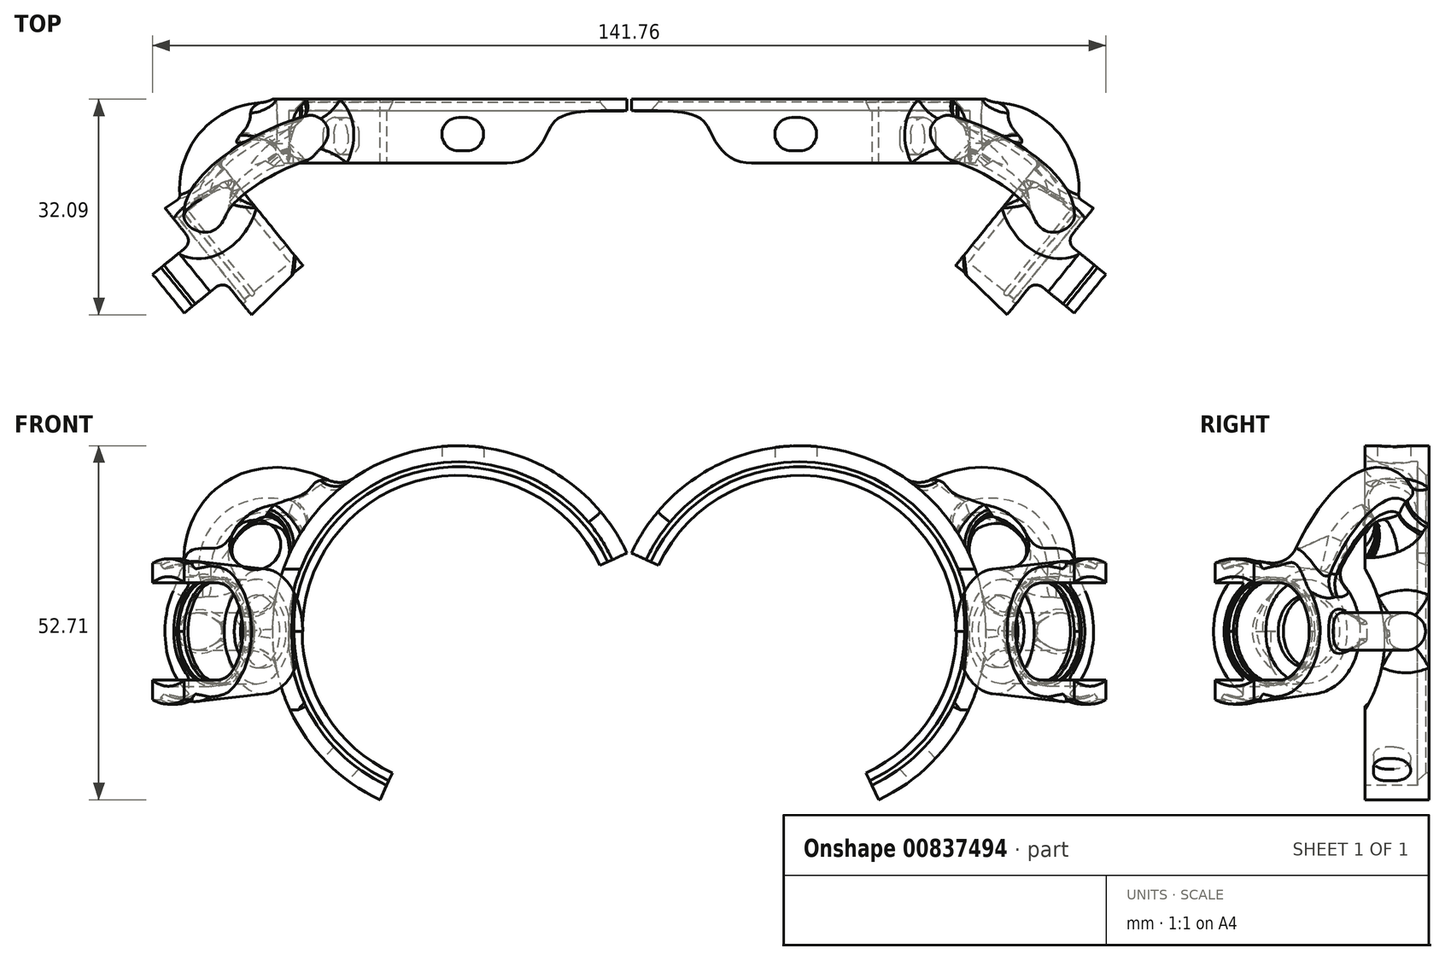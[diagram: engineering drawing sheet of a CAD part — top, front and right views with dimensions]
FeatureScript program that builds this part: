
annotation { "Feature Type Name" : "Feature", "Feature Type Description" : "" }
export const myFeature = defineFeature(function(context is Context, id is Id, definition is map)
    precondition{}
    {
        {
            var Q0;
            Q0=qCreatedBy(makeId("Front.planeOp"),FACE);
            var sketch = newSketch(context, id + "F0", { "sketchPlane" : qUnion([Q0])});
            skCircle(sketch, "E0", {"center": v(0, 0) * mm, "radius": 25.27 * mm, "construction": true});
            skCircle(sketch, "E1", {"center": v(0, 0) * mm, "radius": 23.24 * mm, "construction": true});
            skLineSegment(sketch, "E2", {"start": v(0, 0) * mm, "end": v(0, 25.27) * mm, "construction": true});
            skLineSegment(sketch, "E3", {"start": v(0, 0) * mm, "end": v(25.27, 0) * mm, "construction": true});
            skLineSegment(sketch, "E4", {"start": v(0, 0) * mm, "end": v(17.87, 17.87) * mm, "construction": true});
            skCircle(sketch, "E5", {"center": v(0, 0) * mm, "radius": 15.88 * mm, "construction": true});
            skPoint(sketch, "E6", {"position": v(17.87, 17.86) * mm});
            skLineSegment(sketch, "E7", {"start": v(0, 0) * mm, "end": v(16.74, -18.92) * mm, "construction": true});
            skPoint(sketch, "E8", {"position": v(17.88, -17.85) * mm});
            skSolve(sketch);
        }
        {
            var Q0;
            Q0=qCreatedBy(makeId("Right.planeOp"),FACE);
            var sketch = newSketch(context, id + "F1", { "sketchPlane" : qUnion([Q0])});
            skLineSegment(sketch, "E9.0", {"start": v(0, -25.27) * mm, "end": v(0, 25.27) * mm, "construction": true});
            skLineSegment(sketch, "E9.1", {"start": v(0, -23.24) * mm, "end": v(0, 23.24) * mm, "construction": true});
            skLineSegment(sketch, "E10", {"start": v(0, 23.24) * mm, "end": v(-1.73, 23.24) * mm});
            skLineSegment(sketch, "E11", {"start": v(-1.73, 23.24) * mm, "end": v(-1.73, 25.27) * mm});
            skLineSegment(sketch, "E12", {"start": v(-1.73, 25.27) * mm, "end": v(-9.53, 25.27) * mm});
            skLineSegment(sketch, "E13", {"start": v(0, 23.24) * mm, "end": v(0, 25.27) * mm});
            skLineSegment(sketch, "E14", {"start": v(-9.53, 25.27) * mm, "end": v(-9.53, 27.65) * mm});
            skLineSegment(sketch, "E15", {"start": v(-9.53, 27.65) * mm, "end": v(0, 27.65) * mm});
            skLineSegment(sketch, "E16", {"start": v(0, 27.65) * mm, "end": v(0, 25.27) * mm});
            skLineSegment(sketch, "E17", {"start": v(0, 0) * mm, "end": v(1.7, 0) * mm, "construction": true});
            skLineSegment(sketch, "E18.0", {"start": v(0, -15.88) * mm, "end": v(0, 15.88) * mm, "construction": true});
            skLineSegment(sketch, "E19", {"start": v(0, 15.88) * mm, "end": v(5.77, 15.88) * mm, "construction": true});
            skLineSegment(sketch, "E20", {"start": v(0, -15.88) * mm, "end": v(5.77, -15.88) * mm, "construction": true});
            skLineSegment(sketch, "E21", {"start": v(0, 27.65) * mm, "end": v(-14.29, 27.65) * mm, "construction": true});
            skLineSegment(sketch, "E22", {"start": v(0, -25.27) * mm, "end": v(-14.29, -25.27) * mm, "construction": true});
            skLineSegment(sketch, "E23", {"start": v(5.77, 15.88) * mm, "end": v(5.77, -15.88) * mm, "construction": true});
            skLineSegment(sketch, "E24", {"start": v(6.02, 0) * mm, "end": v(18.72, 0) * mm});
            skPoint(sketch, "E25", {"position": v(-5.16, 27.65) * mm});
            skSolve(sketch);
        }
        {
            var Q0;
            Q0=makeQuery(id+"F1.imprint","IMPRINT",FACE,{"disambiguationData":[TD([[makeQuery(id+"F1.imprint","IMPRINT",EDGE,{"derivedFrom":sQuery(id+"F1.wireOp",EDGE,"E10")}),-1.0]])]});
            var Q1;
            Q1=sQuery(id+"F1.wireOp",EDGE,"E17");
            revolve(context, id + "F2", {"surfaceOperationType" : NewSurfaceOperationType.NEW, "entities" : qUnion([Q0]), "axis" : qUnion([Q1]), "revolveType" : RevolveType.TWO_DIRECTIONS, "angle" : 115 * degree, "angleBack" : 310 * degree});
        }
        {
            var Q0;
            Q0=qCreatedBy(makeId("Top.planeOp"),FACE);
            var sketch = newSketch(context, id + "F3", { "sketchPlane" : qUnion([Q0])});
            skLineSegment(sketch, "E26.0", {"start": v(0, 6.02) * mm, "end": v(0, 18.72) * mm});
            skLineSegment(sketch, "E26.1.0", {"start": v(-21.18, -9.53) * mm, "end": v(27.65, -9.53) * mm});
            skLineSegment(sketch, "E26.1.1", {"start": v(25.06, -9.53) * mm, "end": v(25.06, 0) * mm});
            skLineSegment(sketch, "E26.1.2", {"start": v(27.65, 0) * mm, "end": v(-21.18, 0) * mm});
            skLineSegment(sketch, "E26.1.3", {"start": v(-21.18, 0) * mm, "end": v(-21.18, -9.53) * mm});
            skLineSegment(sketch, "E27", {"start": v(0, 6.02) * mm, "end": v(4.9, 12.06) * mm, "construction": true});
            skLineSegment(sketch, "E28", {"start": v(0, 6.02) * mm, "end": v(25.06, -14.29) * mm, "construction": true});
            skLineSegment(sketch, "E29", {"start": v(4.9, 12.06) * mm, "end": v(34.84, -12.22) * mm, "construction": true});
            skLineSegment(sketch, "E30", {"start": v(25.06, -9.53) * mm, "end": v(25.06, -19.05) * mm, "construction": true});
            skLineSegment(sketch, "E31.MirrorCS", {"start": v(-4.9, -0.02) * mm, "end": v(25.06, -24.3) * mm, "construction": true});
            skLineSegment(sketch, "E32.MirrorCS", {"start": v(0, 6.02) * mm, "end": v(-4.9, -0.02) * mm, "construction": true});
            skLineSegment(sketch, "E33", {"start": v(25.06, -19.05) * mm, "end": v(25.06, -24.3) * mm});
            skLineSegment(sketch, "E34", {"start": v(25.06, -24.3) * mm, "end": v(34.84, -12.22) * mm, "construction": true});
            skLineSegment(sketch, "E35", {"start": v(34.84, -12.22) * mm, "end": v(33.35, -14.07) * mm});
            skLineSegment(sketch, "E36", {"start": v(33.35, -14.07) * mm, "end": v(32.42, -13.32) * mm});
            skLineSegment(sketch, "E37", {"start": v(34.84, -12.22) * mm, "end": v(41.63, -17.71) * mm});
            skLineSegment(sketch, "E38", {"start": v(41.63, -17.71) * mm, "end": v(42.59, -16.53) * mm});
            skLineSegment(sketch, "E39", {"start": v(42.59, -16.53) * mm, "end": v(34.88, -10.28) * mm});
            skLineSegment(sketch, "E40", {"start": v(32.42, -13.32) * mm, "end": v(34.88, -10.28) * mm});
            skLineSegment(sketch, "E41", {"start": v(41.87, -17.42) * mm, "end": v(48.28, -22.61) * mm});
            skLineSegment(sketch, "E42", {"start": v(42.59, -16.53) * mm, "end": v(49, -21.73) * mm});
            skLineSegment(sketch, "E43", {"start": v(48.28, -22.61) * mm, "end": v(49, -21.73) * mm});
            skLineSegment(sketch, "E44", {"start": v(29.95, -18.25) * mm, "end": v(32.08, -19.98) * mm, "construction": true});
            skLineSegment(sketch, "E45", {"start": v(49, -21.73) * mm, "end": v(49.96, -20.54) * mm});
            skLineSegment(sketch, "E46", {"start": v(49.96, -20.54) * mm, "end": v(48.73, -19.54) * mm});
            skLineSegment(sketch, "E47", {"start": v(48.73, -19.54) * mm, "end": v(47.77, -20.73) * mm});
            skLineSegment(sketch, "E48", {"start": v(34.76, -12.31) * mm, "end": v(41.63, -17.71) * mm});
            skLineSegment(sketch, "E49", {"start": v(45.1, -18.57) * mm, "end": v(45.82, -17.68) * mm});
            skLineSegment(sketch, "E50", {"start": v(45.82, -17.68) * mm, "end": v(34.88, -10.28) * mm});
            skCircle(sketch, "E51", {"center": v(40.5, -16.8) * mm, "radius": 0.37 * mm});
            skLineSegment(sketch, "E52", {"start": v(45.82, -17.68) * mm, "end": v(48.17, -20.23) * mm});
            skSolve(sketch);
        }
        {
            var Q0;
            Q0=makeQuery(id+"F3.imprint","IMPRINT",FACE,{"disambiguationData":[TD([[makeQuery(id+"F3.imprint","IMPRINT",EDGE,{"derivedFrom":sQuery(id+"F3.wireOp",EDGE,"E35")}),-1.0]])]});
            var Q1;
            {var subQ2=sQuery(id+"F3.wireOp",EDGE,"E41");Q1=makeQuery(id+"F3.imprint","IMPRINT",FACE,{"disambiguationData":[TD([[makeQuery(id+"F3.imprint","IMPRINT",EDGE,{"derivedFrom":subQ2}),1.0]])]});}
            var Q2;
            {var subQ0=sQuery(id+"F3.wireOp",EDGE,"E45");Q2=makeQuery(id+"F3.imprint","IMPRINT",FACE,{"disambiguationData":[TD([[makeQuery(id+"F3.imprint","IMPRINT",EDGE,{"derivedFrom":subQ0}),1.0]])]});}
            var Q3;
            {var subQ0=sQuery(id+"F3.wireOp",EDGE,"ZS8Crhrf-CrOi-06I2-Trp5-8wOd5zCYoBhE");Q3=makeQuery(id+"F3.imprint","IMPRINT",FACE,{"disambiguationData":[TD([[makeQuery(id+"F3.imprint","IMPRINT",EDGE,{"derivedFrom":subQ0}),-1.0]])]});}
            var Q4;
            {var subQ0=sQuery(id+"F3.wireOp",EDGE,"E39");Q4=makeQuery(id+"F3.imprint","IMPRINT",FACE,{"disambiguationData":[TD([[makeQuery(id+"F3.imprint","IMPRINT",EDGE,{"derivedFrom":subQ0}),-1.0]])]});}
            var Q5;
            {var subQ0=sQuery(id+"F3.wireOp",EDGE,"E51");var subQ1=sQuery(id+"F3.wireOp",EDGE,"E37");var subQ2=makeQuery(id+"F3.imprint","INTERSECT",VERTEX,{"disambiguationData":[OD(0.0)],"derivedFrom":[subQ1,subQ0]});Q5=makeQuery(id+"F3.imprint","IMPRINT",FACE,{"disambiguationData":[TD([[makeQuery(id+"F3.imprint","IMPRINT",EDGE,{"disambiguationData":[TD([[subQ2,-1.0]])],"derivedFrom":subQ1}),1.0]])]});}
            var Q6;
            {var subQ5=sQuery(id+"F3.wireOp",EDGE,"J8IAMYAS-e4tZ-yNnO-T2ef-1q77QjKvg4NF");Q6=makeQuery(id+"F3.imprint","IMPRINT",FACE,{"disambiguationData":[TD([[makeQuery(id+"F3.imprint","IMPRINT",EDGE,{"derivedFrom":subQ5}),-1.0]])]});}
            var Q7;
            {var subQ3=sQuery(id+"F3.wireOp",EDGE,"E49");Q7=makeQuery(id+"F3.imprint","IMPRINT",FACE,{"disambiguationData":[TD([[makeQuery(id+"F3.imprint","IMPRINT",EDGE,{"derivedFrom":subQ3}),-1.0]])]});}
            var Q8;
            Q8=sQuery(id+"F3.wireOp",EDGE,"E44");
            var Q9;
            Q9=sQuery(id+"F3.wireOp",EDGE,"E44");
            revolve(context, id + "F4", {"operationType" : NewBodyOperationType.ADD, "surfaceOperationType" : NewSurfaceOperationType.NEW, "entities" : qUnion([Q0, Q1, Q2, Q3, Q4, Q5, Q6, Q7]), "surfaceEntities" : qUnion([Q8]), "axis" : qUnion([Q9]), "revolveType" : RevolveType.FULL});
        }
        {
            var Q0;
            Q0=makeQuery(id+"F4.opRevolve","SWEPT_FACE",FACE,{"disambiguationData":[OSD([sQuery(id+"F3.wireOp",EDGE,"E35")])]});
            var sketch = newSketch(context, id + "F5", { "sketchPlane" : qUnion([Q0])});
            skCircle(sketch, "E53.0", {"center": v(4.68, 0) * mm, "radius": 5.4 * mm, "construction": true});
            skLineSegment(sketch, "E54", {"start": v(4.68, 0) * mm, "end": v(4.68, 5.4) * mm, "construction": true});
            skLineSegment(sketch, "E55", {"start": v(4.68, 0) * mm, "end": v(6.74, 4.98) * mm, "construction": true});
            skSolve(sketch);
        }
        {
            var Q0;
            Q0=qCreatedBy(makeId("Right.planeOp"),FACE);
            var sketch = newSketch(context, id + "F6", { "sketchPlane" : qUnion([Q0])});
            skEllipse(sketch, "E56.0", {"center": v(-17.5, 0) * mm, "majorRadius": 8.76 * mm, "minorRadius": 5.18 * mm, "majorAxis": v(0, -1), "construction": true});
            skLineSegment(sketch, "E56.1.0", {"start": v(-9.53, 27.65) * mm, "end": v(-9.53, -11.68) * mm, "construction": true});
            skLineSegment(sketch, "E56.1.1", {"start": v(-9.53, -11.68) * mm, "end": v(0, -11.68) * mm});
            skLineSegment(sketch, "E56.1.2", {"start": v(0, -11.68) * mm, "end": v(0, 27.65) * mm});
            skLineSegment(sketch, "E56.1.3", {"start": v(0, 17.77) * mm, "end": v(-9.53, 17.77) * mm, "construction": true});
            skLineSegment(sketch, "E57", {"start": v(-17.5, 0) * mm, "end": v(-9.53, 0) * mm, "construction": true});
            skLineSegment(sketch, "E58", {"start": v(-17.5, 9.3) * mm, "end": v(-9.53, 9.3) * mm, "construction": true});
            skLineSegment(sketch, "E59", {"start": v(-17.5, -9.3) * mm, "end": v(-9.53, -9.3) * mm, "construction": true});
            skLineSegment(sketch, "E60", {"start": v(-9.53, 9.3) * mm, "end": v(-9.53, -9.3) * mm});
            skArc(sketch, "E61", {"start": v(-9.52, -11.68) * mm, "mid": v(-6.6, -1.2) * mm, "end": v(-9.52, 9.3) * mm});
            skLineSegment(sketch, "E62", {"start": v(-9.53, -9.3) * mm, "end": v(-9.53, -11.68) * mm});
            skSolve(sketch);
        }
        {
            var Q0;
            Q0=makeQuery(id+"F6.imprint","IMPRINT",FACE,{"disambiguationData":[TD([[makeQuery(id+"F6.imprint","IMPRINT",EDGE,{"derivedFrom":sQuery(id+"F6.wireOp",EDGE,"GxEW9ax0-zjAY-ybk5-duMN-0JDvZg63hfbD")}),1.0]])]});
            var Q1;
            Q1=makeQuery(id+"F6.imprint","IMPRINT",FACE,{"disambiguationData":[TD([[makeQuery(id+"F6.imprint","IMPRINT",EDGE,{"derivedFrom":sQuery(id+"F6.wireOp",EDGE,"E60")}),1.0]])]});
            extrude(context, id + "F7", {"entities" : qUnion([Q0, Q1]), "operationType" : NewBodyOperationType.REMOVE, "depth" : 50.57 * mm, "offsetDistance" : 25.4 * mm});
        }
        {
            var Q0;
            Q0=qCreatedBy(makeId("Top.planeOp"),FACE);
            var sketch = newSketch(context, id + "F8", { "sketchPlane" : qUnion([Q0])});
            skLineSegment(sketch, "E63.1.0", {"start": v(-21.18, -9.53) * mm, "end": v(26.26, -9.53) * mm, "construction": true});
            skLineSegment(sketch, "E63.1.2", {"start": v(25.06, -11.07) * mm, "end": v(25.06, 0) * mm, "construction": true});
            skLineSegment(sketch, "E63.1.3", {"start": v(27.65, 0) * mm, "end": v(-21.18, 0) * mm, "construction": true});
            skLineSegment(sketch, "E63.1.4", {"start": v(-21.18, 0) * mm, "end": v(-21.18, -9.53) * mm});
            skLineSegment(sketch, "E64.0", {"start": v(25.63, -21.7) * mm, "end": v(32.42, -13.32) * mm, "construction": true});
            skLineSegment(sketch, "E64.1", {"start": v(23.17, -24.73) * mm, "end": v(34.88, -10.28) * mm, "construction": true});
            skLineSegment(sketch, "E64.3", {"start": v(31.84, -29.79) * mm, "end": v(41.63, -17.71) * mm, "construction": true});
            skLineSegment(sketch, "E64.4", {"start": v(25.06, -24.3) * mm, "end": v(34.84, -12.22) * mm, "construction": true});
            skLineSegment(sketch, "E65", {"start": v(34.84, -12.22) * mm, "end": v(41.63, -17.71) * mm, "construction": true});
            skPoint(sketch, "E66", {"position": v(25.06, -3.81) * mm});
            skPoint(sketch, "E66.positionSnap0", {"position": v(27.71, -3.81) * mm});
            skArc(sketch, "E67", {"start": v(38.8, -14.27) * mm, "mid": v(34.84, -5.22) * mm, "end": v(25.06, -3.81) * mm});
            skLineSegment(sketch, "E68", {"start": v(34.84, -12.22) * mm, "end": v(35.4, -11.52) * mm});
            skLineSegment(sketch, "E69", {"start": v(35.4, -11.52) * mm, "end": v(42.19, -17.02) * mm});
            skLineSegment(sketch, "E70", {"start": v(42.19, -17.02) * mm, "end": v(41.63, -17.71) * mm});
            skSolve(sketch);
        }
        {
            var Q0;
            Q0=sQuery(id+"F8.wireOp",EDGE,"E63.1.2");
            cPlane(context, id + "F9", {"entities" : qUnion([Q0]), "cplaneType" : CPlaneType.LINE_ANGLE, "offset" : 25.4 * mm, "angle" : 90 * degree, "width" : 152.4 * mm, "height" : 152.4 * mm});
        }
        {
            var Q0;
            Q0=qCreatedBy(id+"F9.planeOp",FACE);
            var sketch = newSketch(context, id + "F10", { "sketchPlane" : qUnion([Q0])});
            skPoint(sketch, "E71.0", {"position": v(-3.81, 0) * mm});
            skCircle(sketch, "E72", {"center": v(-3.81, 0) * mm, "radius": 2.8 * mm});
            skSolve(sketch);
        }
        {
            var Q0;
            Q0=qSketchRegion(id+"F10",true);
            var Q1;
            Q1=sQuery(id+"F8.wireOp",EDGE,"E67");
            sweep(context, id + "F11", {"operationType" : NewBodyOperationType.ADD, "profiles" : qUnion([Q0]), "path" : qUnion([Q1])});
        }
        {
            var Q0;
            Q0=makeQuery(id+"F2.opRevolve","SWEPT_FACE",FACE,{"disambiguationData":[OSD([sQuery(id+"F1.wireOp",EDGE,"E11")])]});
            var sketch = newSketch(context, id + "F12", { "sketchPlane" : qUnion([Q0])});
            skPoint(sketch, "E73.0", {"position": v(17.87, 17.86) * mm});
            skSolve(sketch);
        }
        {
            var Q0;
            Q0=sQuery(id+"F12.wireOp",VERTEX,"E73.0");
            var Q1;
            Q1=sQuery(id+"F0.wireOp",VERTEX,"E4.end");
            var Q2;
            Q2=sQuery(id+"F0.wireOp",VERTEX,"E6");
            cPlane(context, id + "F13", {"entities" : qUnion([Q0, Q1, Q2]), "cplaneType" : CPlaneType.THREE_POINT, "offset" : 25.4 * mm, "width" : 152.4 * mm, "height" : 152.4 * mm});
        }
        {
            var Q0;
            Q0=qCreatedBy(id+"F13.planeOp",FACE);
            var sketch = newSketch(context, id + "F14", { "sketchPlane" : qUnion([Q0])});
            skLineSegment(sketch, "E74", {"start": v(0, 0) * mm, "end": v(-9.53, 0) * mm, "construction": true});
            skLineSegment(sketch, "E75.0", {"start": v(-9.53, -5.93) * mm, "end": v(-9.53, 27.65) * mm, "construction": true});
            skCircle(sketch, "E76", {"center": v(-4.76, 0) * mm, "radius": 3.18 * mm});
            skLineSegment(sketch, "E77", {"start": v(-4.76, 0) * mm, "end": v(-4.76, 3.18) * mm, "construction": true});
            skLineSegment(sketch, "E78", {"start": v(-4.76, 3.18) * mm, "end": v(-4.76, -3.18) * mm, "construction": true});
            skCircle(sketch, "E79", {"center": v(-4.76, -3.18) * mm, "radius": 1.59 * mm});
            skSolve(sketch);
        }
        {
            var Q0;
            Q0=sQuery(id+"F14.wireOp",EDGE,"E74");
            cPoint(context, id + "F15", {"entities" : qUnion([Q0]), "parameter" : 0.5});
        }
        {
            var Q0;
            Q0=qCreatedBy(id+"F15",VERTEX);
            var Q1;
            Q1=sQuery(id+"F5.wireOp",VERTEX,"E54.start");
            var Q2;
            Q2=sQuery(id+"F5.wireOp",VERTEX,"E55.end");
            cPlane(context, id + "F16", {"entities" : qUnion([Q0, Q1, Q2]), "cplaneType" : CPlaneType.THREE_POINT, "offset" : 25.4 * mm, "width" : 152.4 * mm, "height" : 152.4 * mm});
        }
        {
            var Q0;
            Q0=qCreatedBy(id+"F16.planeOp",FACE);
            var sketch = newSketch(context, id + "F17", { "sketchPlane" : qUnion([Q0])});
            skPoint(sketch, "E80.0", {"position": v(-20.97, 14.4) * mm});
            skArc(sketch, "E81", {"start": v(-20.97, 14.4) * mm, "mid": v(-36.67, 14.03) * mm, "end": v(-42.1, -0.7) * mm});
            skEllipse(sketch, "E82.0", {"center": v(-34.09, -7.39) * mm, "majorRadius": 7.62 * mm, "minorRadius": 1.65 * mm, "majorAxis": v(0.26, -0.97), "construction": true});
            skEllipse(sketch, "E82.1", {"center": v(-45.34, -10.43) * mm, "majorRadius": 10.03 * mm, "minorRadius": 2.17 * mm, "majorAxis": v(0.26, -0.97), "construction": true});
            skLineSegment(sketch, "E83", {"start": v(-36.12, 0.12) * mm, "end": v(-48.07, -0.36) * mm, "construction": true});
            skPoint(sketch, "E84", {"position": v(-42.1, -0.12) * mm});
            skSolve(sketch);
        }
        {
            var Q0;
            Q0=qSketchRegion(id+"F14",true);
            var Q1;
            Q1=sQuery(id+"F17.wireOp",EDGE,"E81");
            sweep(context, id + "F18", {"operationType" : NewBodyOperationType.ADD, "profiles" : qUnion([Q0]), "path" : qUnion([Q1])});
        }
        {
            var Q0;
            Q0=qCreatedBy(makeId("Top.planeOp"),FACE);
            var sketch = newSketch(context, id + "F19", { "sketchPlane" : qUnion([Q0])});
            skLineSegment(sketch, "E85.0", {"start": v(31.6, -30.09) * mm, "end": v(41.87, -17.42) * mm, "construction": true});
            skLineSegment(sketch, "E86.0", {"start": v(22.9, -1.73) * mm, "end": v(22.9, -1.73) * mm});
            skLineSegment(sketch, "E87.0", {"start": v(-21.18, -9.53) * mm, "end": v(-21.18, 0) * mm, "construction": true});
            skLineSegment(sketch, "E87.1", {"start": v(-7.2, -9.53) * mm, "end": v(-21.18, -9.53) * mm, "construction": true});
            skLineSegment(sketch, "E88", {"start": v(-21.18, -1.73) * mm, "end": v(-25.57, -1.73) * mm});
            skLineSegment(sketch, "E89", {"start": v(-25.57, -1.73) * mm, "end": v(-25.57, -14.68) * mm});
            skLineSegment(sketch, "E90", {"start": v(-25.57, -14.68) * mm, "end": v(-7.2, -14.68) * mm});
            skLineSegment(sketch, "E91", {"start": v(-7.2, -14.68) * mm, "end": v(-7.2, -9.53) * mm});
            skFitSpline(sketch, "E92", {"points": [v(41.87, -17.42) * mm, v(35.6, -32.32) * mm, v(36.33, -37.36) * mm], "startDerivative": vector(-14.07, -17.37) * mm, "endDerivative": vector(-39.72, -35.09) * mm, "construction": true});
            skLineSegment(sketch, "E93", {"start": v(41.87, -17.42) * mm, "end": v(44.14, -15.47) * mm});
            skLineSegment(sketch, "E94", {"start": v(44.14, -15.47) * mm, "end": v(53.33, -26.22) * mm});
            skLineSegment(sketch, "E95", {"start": v(53.33, -26.22) * mm, "end": v(38.1, -39.23) * mm});
            skLineSegment(sketch, "E96", {"start": v(38.1, -39.23) * mm, "end": v(36.33, -37.36) * mm});
            skFitSpline(sketch, "E97", {"points": [v(-21.18, -1.73) * mm, v(-12.95, -5.57) * mm, v(-7.2, -9.53) * mm], "startDerivative": vector(39.3, 0) * mm, "endDerivative": vector(20.69, 0) * mm});
            skSolve(sketch);
        }
        {
            var Q0;
            Q0=qSketchRegion(id+"F19",true);
            extrude(context, id + "F20", {"entities" : qUnion([Q0]), "operationType" : NewBodyOperationType.REMOVE, "endBound" : BoundingType.SYMMETRIC, "oppositeDirection" : true, "depth" : 82.8 * mm, "offsetDistance" : 25.4 * mm});
        }
        {
            var Q0;
            Q0=qCreatedBy(makeId("Top.planeOp"),FACE);
            var sketch = newSketch(context, id + "F21", { "sketchPlane" : qUnion([Q0])});
            skCircle(sketch, "E98", {"center": v(0, -5.2) * mm, "radius": 2.48 * mm});
            skCircle(sketch, "E99", {"center": v(-1.27, -5.2) * mm, "radius": 2.48 * mm});
            skLineSegment(sketch, "E100", {"start": v(-1.27, -2.73) * mm, "end": v(0, -2.73) * mm});
            skLineSegment(sketch, "E101", {"start": v(-1.27, -7.68) * mm, "end": v(0, -7.68) * mm});
            skSolve(sketch);
        }
        {
            var Q0;
            Q0=makeQuery(id+"F21.imprint","IMPRINT",FACE,{"disambiguationData":[TD([[makeQuery(id+"F21.imprint","IMPRINT",EDGE,{"derivedFrom":sQuery(id+"F21.wireOp",EDGE,"E98")}),1.0]])]});
            var Q1;
            {var subQ0=sQuery(id+"F21.wireOp",EDGE,"E99");var subQ1=sQuery(id+"F21.wireOp",EDGE,"E98");var subQ2=makeQuery(id+"F21.imprint","INTERSECT",VERTEX,{"disambiguationData":[OD(0.0)],"derivedFrom":[subQ1,subQ0]});Q1=makeQuery(id+"F21.imprint","IMPRINT",FACE,{"disambiguationData":[TD([[makeQuery(id+"F21.imprint","IMPRINT",EDGE,{"disambiguationData":[TD([[subQ2,-1.0]])],"derivedFrom":subQ1}),-1.0]])]});}
            var Q2;
            {var subQ0=sQuery(id+"F21.wireOp",EDGE,"E99");var subQ1=sQuery(id+"F21.wireOp",EDGE,"E98");var subQ2=makeQuery(id+"F21.imprint","INTERSECT",VERTEX,{"disambiguationData":[OD(0.0)],"derivedFrom":[subQ1,subQ0]});Q2=makeQuery(id+"F21.imprint","IMPRINT",FACE,{"disambiguationData":[TD([[makeQuery(id+"F21.imprint","IMPRINT",EDGE,{"disambiguationData":[TD([[subQ2,-1.0]])],"derivedFrom":subQ1}),1.0]])]});}
            var Q3;
            {var subQ0=sQuery(id+"F21.wireOp",EDGE,"E100");Q3=makeQuery(id+"F21.imprint","IMPRINT",FACE,{"disambiguationData":[TD([[makeQuery(id+"F21.imprint","IMPRINT",EDGE,{"derivedFrom":subQ0}),-1.0]])]});}
            var Q4;
            {var subQ0=sQuery(id+"F21.wireOp",EDGE,"E101");Q4=makeQuery(id+"F21.imprint","IMPRINT",FACE,{"disambiguationData":[TD([[makeQuery(id+"F21.imprint","IMPRINT",EDGE,{"derivedFrom":subQ0}),1.0]])]});}
            extrude(context, id + "F22", {"entities" : qUnion([Q0, Q1, Q2, Q3, Q4]), "operationType" : NewBodyOperationType.REMOVE, "depth" : 31.5 * mm, "offsetDistance" : 25.4 * mm});
        }
        {
            var Q0;
            Q0=makeQuery(id+"F2.opRevolve","SWEPT_FACE",FACE,{"disambiguationData":[OSD([sQuery(id+"F1.wireOp",EDGE,"E11")])]});
            var sketch = newSketch(context, id + "F23", { "sketchPlane" : qUnion([Q0])});
            skArc(sketch, "E102.0", {"start": v(22.9, -10.68) * mm, "mid": v(24.44, -6.4) * mm, "end": v(25.2, -1.9) * mm});
            skCircle(sketch, "E103", {"center": v(0, 0) * mm, "radius": 24.48 * mm});
            skArc(sketch, "E104.0", {"start": v(25.2, 1.9) * mm, "mid": v(-25.27, 0) * mm, "end": v(25.2, -1.9) * mm});
            skPoint(sketch, "E105.0", {"position": v(17.87, 17.86) * mm});
            skCircle(sketch, "E106", {"center": v(0, 0) * mm, "radius": 25.27 * mm});
            skSolve(sketch);
        }
        {
            var Q0;
            {var subQ1=sQuery(id+"F1.wireOp",EDGE,"E11");var subQ6=makeQuery(id+"F2.opRevolve","SWEPT_EDGE",EDGE,{"disambiguationData":[OSD([sQuery(id+"F1.wireOp",EDGE,"E10"),subQ1])]});Q0=makeQuery(id+"F23.imprint","IMPRINT",FACE,{"disambiguationData":[TD([[makeQuery(id+"F23.imprint","IMPRINT",EDGE,{"derivedFrom":subQ6}),1.0]])]});}
            var Q1;
            {var subQ1=sQuery(id+"F1.wireOp",EDGE,"E11");var subQ6=makeQuery(id+"F2.opRevolve","SWEPT_EDGE",EDGE,{"disambiguationData":[OSD([sQuery(id+"F1.wireOp",EDGE,"E10"),subQ1])]});Q1=makeQuery(id+"F23.imprint","IMPRINT",FACE,{"disambiguationData":[TD([[makeQuery(id+"F23.imprint","IMPRINT",EDGE,{"derivedFrom":subQ6}),-1.0]])]});}
            extrude(context, id + "F24", {"entities" : qUnion([Q0, Q1]), "operationType" : NewBodyOperationType.REMOVE, "depth" : 43.43 * mm, "offsetDistance" : 25.4 * mm});
        }
        {
            var Q0;
            Q0=makeQuery(id+"F2.opRevolve","CAP_FACE",FACE,{"disambiguationData":[OSD([sQuery(id+"F1.wireOp",EDGE,"E10"),sQuery(id+"F1.wireOp",EDGE,"E11"),sQuery(id+"F1.wireOp",EDGE,"E12"),sQuery(id+"F1.wireOp",EDGE,"E13"),sQuery(id+"F1.wireOp",EDGE,"E14"),sQuery(id+"F1.wireOp",EDGE,"E15"),sQuery(id+"F1.wireOp",EDGE,"E16")])],"isStart":false});
            var Q1;
            Q1=sQuery(id+"F1.wireOp",EDGE,"E24");
            revolve(context, id + "F25", {"operationType" : NewBodyOperationType.ADD, "surfaceOperationType" : NewSurfaceOperationType.NEW, "entities" : qUnion([Q0]), "axis" : qUnion([Q1]), "revolveType" : RevolveType.ONE_DIRECTION, "angle" : 40 * degree});
        }
        {
            var Q0;
            {var subQ0=sQuery(id+"F1.wireOp",EDGE,"E11");Q0=makeQuery(id+"F25.boolean.opBoolean","MERGE",FACE,{"derivedFrom":[makeQuery(id+"F2.opRevolve","SWEPT_FACE",FACE,{"disambiguationData":[OSD([subQ0])]}),makeQuery(id+"F25.opRevolve","SWEPT_FACE",FACE,{"disambiguationData":[OSD([subQ0])]})]});}
            var sketch = newSketch(context, id + "F26", { "sketchPlane" : qUnion([Q0])});
            skPoint(sketch, "E107.0", {"position": v(16.74, -18.92) * mm});
            skSolve(sketch);
        }
        {
            var Q0;
            Q0=sQuery(id+"F0.wireOp",VERTEX,"E7.end");
            var Q1;
            Q1=sQuery(id+"F0.wireOp",VERTEX,"E8");
            var Q2;
            Q2=sQuery(id+"F26.wireOp",VERTEX,"E107.0");
            cPlane(context, id + "F27", {"entities" : qUnion([Q0, Q1, Q2]), "cplaneType" : CPlaneType.THREE_POINT, "offset" : 25.4 * mm, "width" : 152.4 * mm, "height" : 152.4 * mm});
        }
        {
            var Q0;
            Q0=qCreatedBy(id+"F27.planeOp",FACE);
            var sketch = newSketch(context, id + "F28", { "sketchPlane" : qUnion([Q0])});
            skCircle(sketch, "E108", {"center": v(-0.78, -5.2) * mm, "radius": 2.48 * mm});
            skPoint(sketch, "E109.0", {"position": v(-0.78, 0) * mm});
            skLineSegment(sketch, "E110.0", {"start": v(-8.67, -9.52) * mm, "end": v(10.23, -9.52) * mm});
            skLineSegment(sketch, "E111", {"start": v(1.7, -5.2) * mm, "end": v(1.7, -9.52) * mm});
            skLineSegment(sketch, "E112", {"start": v(-3.26, -5.2) * mm, "end": v(-3.26, -9.52) * mm});
            skSolve(sketch);
        }
        {
            var Q0;
            Q0=qSketchRegion(id+"F28",true);
            extrude(context, id + "F29", {"entities" : qUnion([Q0]), "operationType" : NewBodyOperationType.REMOVE, "endBound" : BoundingType.SYMMETRIC, "oppositeDirection" : true, "depth" : 25.4 * mm, "offsetDistance" : 25.4 * mm});
        }
        {
            var Q0;
            Q0=makeQuery(id+"F2.opRevolve","CAP_FACE",FACE,{"disambiguationData":[OSD([sQuery(id+"F1.wireOp",EDGE,"E10"),sQuery(id+"F1.wireOp",EDGE,"E11"),sQuery(id+"F1.wireOp",EDGE,"E12"),sQuery(id+"F1.wireOp",EDGE,"E13"),sQuery(id+"F1.wireOp",EDGE,"E14"),sQuery(id+"F1.wireOp",EDGE,"E15"),sQuery(id+"F1.wireOp",EDGE,"E16")])],"isStart":true});
            var Q1;
            Q1=sQuery(id+"F1.wireOp",EDGE,"E24");
            revolve(context, id + "F30", {"operationType" : NewBodyOperationType.ADD, "surfaceOperationType" : NewSurfaceOperationType.NEW, "entities" : qUnion([Q0]), "axis" : qUnion([Q1]), "revolveType" : RevolveType.ONE_DIRECTION, "oppositeDirection" : true, "angle" : 15 * degree});
        }
        {
            var Q0;
            Q0=makeQuery(id+"F24.boolean.opBoolean","COPY",FACE,{"derivedFrom":makeQuery(id+"F24.opExtrude","SWEPT_FACE",FACE,{"disambiguationData":[OSD([sQuery(id+"F23.wireOp",EDGE,"E103")])]})});
            fillet(context, id + "F31", {"entities" : qUnion([Q0]), "radius" : 1.02 * mm, "tangentPropagation" : true, "allowEdgeOverflow" : false});
        }
        {
            var Q0;
            Q0=qSketchRegion(id+"F23",true);
            var Q1;
            {var subQ0=sQuery(id+"F1.wireOp",EDGE,"E11");Q1=makeQuery(id+"F30.boolean.opBoolean","MERGE",FACE,{"derivedFrom":[makeQuery(id+"F25.boolean.opBoolean","MERGE",FACE,{"derivedFrom":[makeQuery(id+"F2.opRevolve","SWEPT_FACE",FACE,{"disambiguationData":[OSD([subQ0])]}),makeQuery(id+"F25.opRevolve","SWEPT_FACE",FACE,{"disambiguationData":[OSD([subQ0])]})]}),makeQuery(id+"F30.opRevolve","SWEPT_FACE",FACE,{"disambiguationData":[OSD([subQ0])]})]});}
            extrude(context, id + "F32", {"entities" : qUnion([Q0, Q1]), "operationType" : NewBodyOperationType.REMOVE, "depth" : 7.87 * mm, "offsetDistance" : 25.4 * mm});
        }
        {
            var Q0;
            Q0=makeQuery(id+"F4.opRevolve","SWEPT_EDGE",EDGE,{"disambiguationData":[OSD([sQuery(id+"F3.wireOp",EDGE,"E47"),sQuery(id+"F3.wireOp",EDGE,"E52")])]});
            chamfer(context, id + "F33", {"entities" : qUnion([Q0]), "width" : 0.5 * mm, "tangentPropagation" : true});
        }
        {
            var Q0;
            Q0=qCreatedBy(makeId("Right.planeOp"),FACE);
            cPlane(context, id + "F34", {"entities" : qUnion([Q0]), "cplaneType" : CPlaneType.OFFSET, "offset" : 25.4 * mm, "oppositeDirection" : true, "width" : 152.4 * mm, "height" : 152.4 * mm});
        }
        {
            var Q0;
            Q0=makeQuery(id+"F4.opRevolve","SWEPT_FACE",FACE,{"disambiguationData":[OSD([sQuery(id+"F3.wireOp",EDGE,"E43"),sQuery(id+"F3.wireOp",EDGE,"E45"),sQuery(id+"F3.wireOp",EDGE,"ZS8Crhrf-CrOi-06I2-Trp5-8wOd5zCYoBhE")])]});
            var sketch = newSketch(context, id + "F35", { "sketchPlane" : qUnion([Q0])});
            skCircle(sketch, "E113.0", {"center": v(4.68, 0) * mm, "radius": 8.15 * mm, "construction": true});
            skLineSegment(sketch, "E114.bottom", {"start": v(17.28, -12.7) * mm, "end": v(8.39, -12.7) * mm});
            skLineSegment(sketch, "E114.top", {"start": v(17.28, 12.7) * mm, "end": v(8.39, 12.7) * mm});
            skLineSegment(sketch, "E114.left", {"start": v(17.28, -12.7) * mm, "end": v(17.28, 12.7) * mm});
            skLineSegment(sketch, "E114.right", {"start": v(8.39, -12.7) * mm, "end": v(8.39, 12.7) * mm});
            skPoint(sketch, "E114.middle", {"position": v(12.83, 0) * mm});
            skLineSegment(sketch, "E115", {"start": v(4.68, 0) * mm, "end": v(4.68, -1) * mm});
            skLineSegment(sketch, "E116.MirrorCS", {"start": v(-7.92, -12.7) * mm, "end": v(-7.92, 12.7) * mm});
            skLineSegment(sketch, "E117.MirrorCS", {"start": v(0.97, -12.7) * mm, "end": v(0.97, 12.7) * mm});
            skLineSegment(sketch, "E118.MirrorCS", {"start": v(-7.92, 12.7) * mm, "end": v(0.97, 12.7) * mm});
            skPoint(sketch, "E119.MirrorP", {"position": v(-3.48, 0) * mm});
            skLineSegment(sketch, "E120.MirrorCS", {"start": v(-7.92, -12.7) * mm, "end": v(0.97, -12.7) * mm});
            skSolve(sketch);
        }
        {
            var Q0;
            Q0=qSketchRegion(id+"F35",true);
            extrude(context, id + "F36", {"entities" : qUnion([Q0]), "operationType" : NewBodyOperationType.REMOVE, "oppositeDirection" : true, "depth" : 7.62 * mm, "offsetDistance" : 25.4 * mm});
        }
        {
            var Q0;
            Q0=makeQuery(id+"F36.boolean.opBoolean","COPY",EDGE,{"disambiguationData":[OD(1.0)],"derivedFrom":makeQuery(id+"F36.opExtrude","CAP_EDGE",EDGE,{"disambiguationData":[OSD([sQuery(id+"F35.wireOp",EDGE,"E114.right")])],"isStart":false})});
            var Q1;
            Q1=makeQuery(id+"F36.boolean.opBoolean","COPY",EDGE,{"disambiguationData":[OD(0.0)],"derivedFrom":makeQuery(id+"F36.opExtrude","CAP_EDGE",EDGE,{"disambiguationData":[OSD([sQuery(id+"F35.wireOp",EDGE,"E114.right")])],"isStart":false})});
            var Q2;
            Q2=makeQuery(id+"F36.boolean.opBoolean","COPY",EDGE,{"disambiguationData":[OD(0.0)],"derivedFrom":makeQuery(id+"F36.opExtrude","CAP_EDGE",EDGE,{"disambiguationData":[OSD([sQuery(id+"F35.wireOp",EDGE,"E117.MirrorCS")])],"isStart":false})});
            var Q3;
            Q3=makeQuery(id+"F36.boolean.opBoolean","COPY",EDGE,{"disambiguationData":[OD(1.0)],"derivedFrom":makeQuery(id+"F36.opExtrude","CAP_EDGE",EDGE,{"disambiguationData":[OSD([sQuery(id+"F35.wireOp",EDGE,"E117.MirrorCS")])],"isStart":false})});
            fillet(context, id + "F37", {"entities" : qUnion([Q0, Q1, Q2, Q3]), "radius" : 1.52 * mm, "tangentPropagation" : true, "allowEdgeOverflow" : false});
        }
        {
            var Q0;
            {var subQ0=sQuery(id+"F3.wireOp",EDGE,"E51");var subQ1=sQuery(id+"F3.wireOp",EDGE,"E48");var subQ2=makeQuery(id+"F3.imprint","INTERSECT",VERTEX,{"disambiguationData":[OD(0.0)],"derivedFrom":[subQ1,subQ0]});Q0=makeQuery(id+"F3.imprint","IMPRINT",FACE,{"disambiguationData":[TD([[makeQuery(id+"F3.imprint","IMPRINT",EDGE,{"disambiguationData":[TD([[subQ2,-1.0]])],"derivedFrom":subQ1}),-1.0]])]});}
            var Q1;
            {var subQ0=sQuery(id+"F3.wireOp",EDGE,"E51");var subQ1=sQuery(id+"F3.wireOp",EDGE,"E37");var subQ2=makeQuery(id+"F3.imprint","INTERSECT",VERTEX,{"disambiguationData":[OD(0.0)],"derivedFrom":[subQ1,subQ0]});Q1=makeQuery(id+"F3.imprint","IMPRINT",FACE,{"disambiguationData":[TD([[makeQuery(id+"F3.imprint","IMPRINT",EDGE,{"disambiguationData":[TD([[subQ2,-1.0]])],"derivedFrom":subQ1}),1.0]])]});}
            var Q2;
            {var subQ0=sQuery(id+"F3.wireOp",EDGE,"E51");var subQ1=sQuery(id+"F3.wireOp",EDGE,"E37");var subQ2=makeQuery(id+"F3.imprint","INTERSECT",VERTEX,{"disambiguationData":[OD(0.0)],"derivedFrom":[subQ1,subQ0]});Q2=makeQuery(id+"F3.imprint","IMPRINT",FACE,{"disambiguationData":[TD([[makeQuery(id+"F3.imprint","IMPRINT",EDGE,{"disambiguationData":[TD([[subQ2,-1.0]])],"derivedFrom":subQ1}),-1.0]])]});}
            var Q3;
            Q3=sQuery(id+"F3.wireOp",EDGE,"E44");
            revolve(context, id + "F38", {"operationType" : NewBodyOperationType.ADD, "surfaceOperationType" : NewSurfaceOperationType.NEW, "entities" : qUnion([Q0, Q1, Q2]), "axis" : qUnion([Q3]), "revolveType" : RevolveType.ONE_DIRECTION, "angle" : 180 * degree});
        }
        {
            var Q0;
            Q0=makeQuery(id+"F11.boolean.opBoolean","INTERSECT",EDGE,{"derivedFrom":[makeQuery(id+"F2.opRevolve","SWEPT_FACE",FACE,{"disambiguationData":[OSD([sQuery(id+"F1.wireOp",EDGE,"E15")])]}),makeQuery(id+"F11.opSweep","SWEPT_FACE",FACE,{"disambiguationData":[OSD([sQuery(id+"F8.wireOp",EDGE,"E67"),sQuery(id+"F10.wireOp",EDGE,"E72")])]})]});
            fillet(context, id + "F39", {"entities" : qUnion([Q0]), "radius" : 4.32 * mm, "tangentPropagation" : true, "allowEdgeOverflow" : false});
        }
        {
            var Q0;
            Q0=makeQuery(id+"F11.boolean.opBoolean","INTERSECT",EDGE,{"derivedFrom":[makeQuery(id+"F4.opRevolve","SWEPT_FACE",FACE,{"disambiguationData":[OSD([sQuery(id+"F3.wireOp",EDGE,"E50")])]}),makeQuery(id+"F11.opSweep","SWEPT_FACE",FACE,{"disambiguationData":[OSD([sQuery(id+"F8.wireOp",EDGE,"E67"),sQuery(id+"F10.wireOp",EDGE,"E72")])]})]});
            fillet(context, id + "F40", {"entities" : qUnion([Q0]), "radius" : 0.76 * mm, "tangentPropagation" : true, "allowEdgeOverflow" : false});
        }
        {
            var Q0;
            {var subQ0=sQuery(id+"F1.wireOp",EDGE,"E11");var subQ1=sQuery(id+"F1.wireOp",EDGE,"E10");Q0=makeQuery(id+"F30.boolean.opBoolean","MERGE",EDGE,{"derivedFrom":[makeQuery(id+"F25.boolean.opBoolean","MERGE",EDGE,{"derivedFrom":[makeQuery(id+"F2.opRevolve","SWEPT_EDGE",EDGE,{"disambiguationData":[OSD([subQ1,subQ0])]}),makeQuery(id+"F25.opRevolve","SWEPT_EDGE",EDGE,{"disambiguationData":[OSD([subQ1,subQ0])]})]}),makeQuery(id+"F30.opRevolve","SWEPT_EDGE",EDGE,{"disambiguationData":[OSD([subQ1,subQ0])]})]});}
            chamfer(context, id + "F41", {"entities" : qUnion([Q0]), "width" : 1.27 * mm, "tangentPropagation" : true});
        }
        {
            var Q0;
            {var subQ0=sQuery(id+"F17.wireOp",EDGE,"E81");var subQ1=sQuery(id+"F14.wireOp",EDGE,"E79");var subQ2=sQuery(id+"F14.wireOp",EDGE,"E76");Q0=makeQuery(id+"F18.opSweep","SWEPT_EDGE",EDGE,{"disambiguationData":[OSD([subQ2,subQ1,subQ0]),TDD([makeQuery(id+"F14.imprint","INTERSECT",VERTEX,{"disambiguationData":[OD(1.0)],"derivedFrom":[subQ2,subQ1]}),subQ0])]});}
            var Q1;
            {var subQ0=sQuery(id+"F17.wireOp",EDGE,"E81");var subQ1=sQuery(id+"F14.wireOp",EDGE,"E79");var subQ2=sQuery(id+"F14.wireOp",EDGE,"E76");Q1=makeQuery(id+"F18.opSweep","SWEPT_EDGE",EDGE,{"disambiguationData":[OSD([subQ2,subQ1,subQ0]),TDD([makeQuery(id+"F14.imprint","INTERSECT",VERTEX,{"disambiguationData":[OD(0.0)],"derivedFrom":[subQ2,subQ1]}),subQ0])]});}
            fillet(context, id + "F42", {"entities" : qUnion([Q0, Q1]), "radius" : 7.62 * mm, "tangentPropagation" : true, "allowEdgeOverflow" : false});
        }
        {
            var Q0;
            {var subQ0=sQuery(id+"F1.wireOp",EDGE,"E15");var subQ1=sQuery(id+"F17.wireOp",EDGE,"E81");var subQ2=sQuery(id+"F14.wireOp",EDGE,"E79");var subQ3=sQuery(id+"F14.wireOp",EDGE,"E76");Q0=makeQuery(id+"F42.opFillet","BLEND_EDGE",EDGE,{"blendedFrom":[makeQuery(id+"F18.opSweep","SWEPT_EDGE",EDGE,{"disambiguationData":[OSD([subQ3,subQ2,subQ1]),TDD([makeQuery(id+"F14.imprint","INTERSECT",VERTEX,{"disambiguationData":[OD(1.0)],"derivedFrom":[subQ3,subQ2]}),subQ1])]}),makeQuery(id+"F39.opFillet","SPLIT",FACE,{"disambiguationData":[OD(0.0)],"derivedFrom":makeQuery(id+"F30.boolean.opBoolean","MERGE",FACE,{"derivedFrom":[makeQuery(id+"F25.boolean.opBoolean","MERGE",FACE,{"derivedFrom":[makeQuery(id+"F2.opRevolve","SWEPT_FACE",FACE,{"disambiguationData":[OSD([subQ0])]}),makeQuery(id+"F25.opRevolve","SWEPT_FACE",FACE,{"disambiguationData":[OSD([subQ0])]})]}),makeQuery(id+"F30.opRevolve","SWEPT_FACE",FACE,{"disambiguationData":[OSD([subQ0])]})]})})],"blendedInto":[makeQuery(id+"F39.opFillet","SPLIT",FACE,{"disambiguationData":[OD(0.0)],"derivedFrom":makeQuery(id+"F30.boolean.opBoolean","MERGE",FACE,{"derivedFrom":[makeQuery(id+"F25.boolean.opBoolean","MERGE",FACE,{"derivedFrom":[makeQuery(id+"F2.opRevolve","SWEPT_FACE",FACE,{"disambiguationData":[OSD([subQ0])]}),makeQuery(id+"F25.opRevolve","SWEPT_FACE",FACE,{"disambiguationData":[OSD([subQ0])]})]}),makeQuery(id+"F30.opRevolve","SWEPT_FACE",FACE,{"disambiguationData":[OSD([subQ0])]})]})})]});}
            var Q1;
            Q1=makeQuery(id+"F18.boolean.opBoolean","INTERSECT",EDGE,{"derivedFrom":[makeQuery(id+"F4.opRevolve","SWEPT_FACE",FACE,{"disambiguationData":[OSD([sQuery(id+"F3.wireOp",EDGE,"E50")])]}),makeQuery(id+"F18.opSweep","SWEPT_FACE",FACE,{"disambiguationData":[OSD([sQuery(id+"F14.wireOp",EDGE,"E76"),sQuery(id+"F17.wireOp",EDGE,"E81")])]})]});
            fillet(context, id + "F43", {"entities" : qUnion([Q0, Q1]), "radius" : 3.8 * mm, "tangentPropagation" : true, "allowEdgeOverflow" : false});
        }
        {
            var Q0;
            Q0=makeQuery(id+"F2.opRevolve","SWEPT_BODY",BODY,{"disambiguationData":[OSD([sQuery(id+"F1.wireOp",EDGE,"E10"),sQuery(id+"F1.wireOp",EDGE,"E11"),sQuery(id+"F1.wireOp",EDGE,"E12"),sQuery(id+"F1.wireOp",EDGE,"E13"),sQuery(id+"F1.wireOp",EDGE,"E14"),sQuery(id+"F1.wireOp",EDGE,"E15"),sQuery(id+"F1.wireOp",EDGE,"E16")])]});
            var Q1;
            Q1=qCreatedBy(id+"F34.planeOp",FACE);
            mirror(context, id + "F44", {"entities" : qUnion([Q0]), "mirrorPlane" : qUnion([Q1])});
        }
        {
            var Q0;
            Q0=makeQuery(id+"F44.opPattern","COPY",FACE,{"derivedFrom":makeQuery(id+"F2.opRevolve","SWEPT_FACE",FACE,{"disambiguationData":[OSD([sQuery(id+"F1.wireOp",EDGE,"E14")])]}),"instanceName":"1"});
            var sketch = newSketch(context, id + "F45", { "sketchPlane" : qUnion([Q0])});
            skArc(sketch, "E121.0", {"start": v(-70.95, -18.93) * mm, "mid": v(-73.7, -15.5) * mm, "end": v(-75.86, -11.68) * mm});
            skArc(sketch, "E121.1", {"start": v(-62.48, -25.06) * mm, "mid": v(-64.94, -23.76) * mm, "end": v(-67.25, -22.22) * mm});
            skArc(sketch, "E121.2", {"start": v(-61.48, -22.9) * mm, "mid": v(-63.6, -21.79) * mm, "end": v(-65.6, -20.48) * mm});
            skArc(sketch, "E121.3", {"start": v(-69.31, -17.2) * mm, "mid": v(-71.76, -14.1) * mm, "end": v(-73.7, -10.68) * mm});
            skPoint(sketch, "E121.4", {"position": v(-73.7, -15.5) * mm});
            skCircle(sketch, "E122", {"center": v(-50.8, 0) * mm, "radius": 27.65 * mm});
            skCircle(sketch, "E123", {"center": v(-50.8, 0) * mm, "radius": 25.27 * mm});
            skLineSegment(sketch, "E124", {"start": v(-62.48, -25.06) * mm, "end": v(-61.48, -22.9) * mm});
            skLineSegment(sketch, "E125", {"start": v(-75.86, -11.68) * mm, "end": v(-73.7, -10.68) * mm});
            skSolve(sketch);
        }
        {
            var Q0;
            {var subQ0=sQuery(id+"F45.wireOp",EDGE,"E124");Q0=makeQuery(id+"F45.imprint","IMPRINT",FACE,{"disambiguationData":[TD([[makeQuery(id+"F45.imprint","IMPRINT",EDGE,{"derivedFrom":subQ0}),1.0]])]});}
            extrude(context, id + "F46", {"entities" : qUnion([Q0]), "operationType" : NewBodyOperationType.ADD, "oppositeDirection" : true, "depth" : 1.27 * mm, "offsetDistance" : 25.4 * mm});
        }
        {
            var Q0;
            Q0=makeQuery(id+"F46.boolean.opBoolean","INTERSECT",EDGE,{"derivedFrom":[makeQuery(id+"F44.opPattern","COPY",FACE,{"derivedFrom":makeQuery(id+"F29.boolean.opBoolean","COPY",FACE,{"derivedFrom":makeQuery(id+"F29.opExtrude","SWEPT_FACE",FACE,{"disambiguationData":[OSD([sQuery(id+"F28.wireOp",EDGE,"E111")])]})}),"instanceName":"1"}),makeQuery(id+"F46.opExtrude","CAP_FACE",FACE,{"disambiguationData":[OSD([sQuery(id+"F45.wireOp",EDGE,"E122"),sQuery(id+"F45.wireOp",EDGE,"E123"),sQuery(id+"F45.wireOp",EDGE,"E124"),sQuery(id+"F45.wireOp",EDGE,"E125")])],"isStart":false})]});
            var Q1;
            Q1=makeQuery(id+"F46.boolean.opBoolean","INTERSECT",EDGE,{"derivedFrom":[makeQuery(id+"F44.opPattern","COPY",FACE,{"derivedFrom":makeQuery(id+"F29.boolean.opBoolean","COPY",FACE,{"derivedFrom":makeQuery(id+"F29.opExtrude","SWEPT_FACE",FACE,{"disambiguationData":[OSD([sQuery(id+"F28.wireOp",EDGE,"E112")])]})}),"instanceName":"1"}),makeQuery(id+"F46.opExtrude","CAP_FACE",FACE,{"disambiguationData":[OSD([sQuery(id+"F45.wireOp",EDGE,"E122"),sQuery(id+"F45.wireOp",EDGE,"E123"),sQuery(id+"F45.wireOp",EDGE,"E124"),sQuery(id+"F45.wireOp",EDGE,"E125")])],"isStart":false})]});
            fillet(context, id + "F47", {"entities" : qUnion([Q0, Q1]), "tangentPropagation" : true, "radius" : 1.78 * mm, "defaultsChanged" : true, "vertexSettings" : [], "allowEdgeOverflow" : false});
        }
        {
            var Q0;
            Q0=makeQuery(id+"F46.opExtrude","CAP_EDGE",EDGE,{"disambiguationData":[OSD([sQuery(id+"F45.wireOp",EDGE,"E125")])],"isStart":true});
            chamfer(context, id + "F48", {"entities" : qUnion([Q0]), "width" : 0.5 * mm, "tangentPropagation" : true});
        }
        {
            var Q0;
            Q0=makeQuery(id+"F44.opPattern","COPY",BODY,{"derivedFrom":makeQuery(id+"F2.opRevolve","SWEPT_BODY",BODY,{"disambiguationData":[OSD([sQuery(id+"F1.wireOp",EDGE,"E10"),sQuery(id+"F1.wireOp",EDGE,"E11"),sQuery(id+"F1.wireOp",EDGE,"E12"),sQuery(id+"F1.wireOp",EDGE,"E13"),sQuery(id+"F1.wireOp",EDGE,"E14"),sQuery(id+"F1.wireOp",EDGE,"E15"),sQuery(id+"F1.wireOp",EDGE,"E16")])]}),"instanceName":"1"});
            var Q1;
            Q1=qCreatedBy(id+"F34.planeOp",FACE);
            mirror(context, id + "F49", {"operationType" : NewBodyOperationType.ADD, "entities" : qUnion([Q0]), "mirrorPlane" : qUnion([Q1])});
        }
    });
